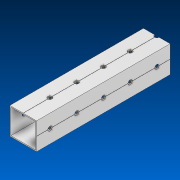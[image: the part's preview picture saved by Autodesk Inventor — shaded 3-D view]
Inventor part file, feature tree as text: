
AUTODESK INVENTOR PART (.ipt)
format: ipt  version: 2022.2 (Build 262287000, 287)  size: 727,552 bytes
history: native  units: in
note: dims shown in document units (in); Inventor stores cm internally (conversion verified against a paired STEP export)
features: other x10, pattern_linear x2, extrude x1, sketch x1
ambient origin geometry x8: Origin, YZ Plane, XZ Plane, XY Plane, X Axis, Y Axis, Z Axis, Center Point
bodies: Solid1 (feature_tree)
feature tree (14):
  extrude  "Extrusion1"  TaperAngle=0.0deg  [1 undecoded]
  other  "Work Axis1"
  other  "Work Axis2"
  pattern_linear  "Rectangular Pattern1"  Count1=5  [1 undecoded]
  pattern_linear  "Rectangular Pattern2"  Spacing1=1.0in  [1 undecoded]
  sketch  "Sketch1"  dims[d0=54.0in d1=0.0in d2=1.9685in d4=1.0in d5=1.5748in d7=1.0in]
  other  "Work Axis3"
  other  "Work Axis4"
  other  "Work Axis5"
  other  "Work Axis6"
  other  "Work Axis7"
  other  "Work Axis8"
  other  "Work Axis63"
  other  "LPattern2"
note: 3 required parameter values undecoded (feature->parameter linkage not recoverable at this tier; creation-order binding heuristic only, values carry confidence <= 0.55)
